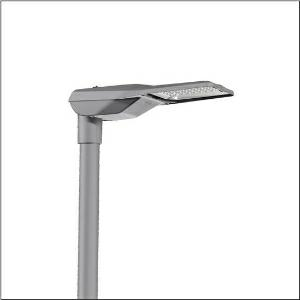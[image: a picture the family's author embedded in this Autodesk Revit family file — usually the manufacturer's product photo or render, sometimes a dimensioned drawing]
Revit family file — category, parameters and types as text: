
# Revit family: streetlight_sl_21_mini___st1_0a_5xe2d33s08hb_eb53
name_source: partatom
category: Lighting Fixtures
units: mm (PartAtom-declared; Revit-internal decimal feet)

## family parameters
Cut with Voids When Loaded = No
Host = Face
Light Source = No
Part Type = Normal
Room Calculation Point = No
Round Connector Dimension = Use Diameter
Shared = No

## types (1)
- --- (1 x LED, 9040 lm, 66 W, 3000K)
    Apparent Load = 66 VA
    CIE Flux Codes = 37 72 97 100 100
    Color Rendering = 70
    Color Temperature = 3000K
    Default Elevation = 1800 mm
    Description = Streetlight SL 21 mini, mast luminaire, primary light control with lens, of PMMA, primary optical cover: cover, of toughened safety glass, transparent, light distribution: ST1.0a, light emission: direct distribution, primary light characteristic: asymmetric, installation type: side-entry, post-top, LED, High Power LED, rated luminous flux: 9.040lm, luminous efficacy: 137lm/W, light colour: 730, colour temperature: 3000K, control gear: D4i, control: flexible luminous flux parameterisation, time-dependent luminous flux control, constant luminous flux control, overheat protection, pre-setting: logarithmic dimming characteristic, mains connection: 220..240V, AC, 50/60Hz, start of lifetime: 66W, end of service life: 69W, reduction: 30W, luminaire housing, of diecast aluminium, powder-coated, SITECO metallic grey (DB 702S), corrosivity category C5 high according to DIN EN ISO 12944, please order mast flange separately, inclination adjustable: 0°, 5°, 10°, 15°, sealing non-destructively replaceable, multi-level sealing system, length: 628mm, width: 235mm, height: 110mm, mast flange for spigot size: 42mm (side-entry): 5XC10008XM4, 60/48mm (side-entry/post-top): 5XC10108XM2, 76/60mm (side-entry/post-top): 5XC10108XM1, mounting height: 4..8m, Smart Interface above, protection rating (complete): IP66, insulation class (complete): insulation class II (safety insulation), certification: CE, ENEC, ENEC+, VDE, impact resistance: IK10, permissible operating ambient temperature for outdoor applications: -40..+50°C, standard-compliant lighting for roads and squares, packaging unit: 1 piece

Light Distribution: ST1.0a
    Height = 110 mm
    Lamp = 1 x LED
    Lamp Light Flux = 9040 lm
    Lamp Power = 66 W
    Lamp count = 1
    Length = 625 mm
    Luminous efficacy = 137 lm/W
    Manufacturer = Siteco
    ModVariant = No
    Model = 5XE2D33S08HB
    Number of Poles = 1
    OnlyDefault = Yes
    Power Factor = 1
    Product Name = Streetlight SL 21 mini | ST1.0a
    Product group = mast luminaire | pylon top
    ProductGroupID = 6100
    Protection Class = Protection class II
    Protection Degree = IP 66
    RLX_Detail_Level = 1
    RLX_Emergency_Light_Flux = 0 lm
    RLX_Emergency_Type = 0
    RLX_Emergency_Type_DB = No
    RlxData = <blob elided: 26157 chars, md5=0b8f44f5>
    Socket = socket
    Standby Power = 0 W
    System Light Flux = 9040 lm
    System Power = 66 W
    Type Comments = factory setting: luminous flux: 100 % | dim-lin: 254 | 670 mA
    Type Image = l_1003515.jpg
    URL = http://relux.com
    VarID = @adj_186119
    Voltage = 0 V
    Weight = 0.00 kg
    Width = 234 mm

## geometry (parser evidence)
native form markers: Blend x4, Sweep x11
no freeform markers — native parametric forms only
